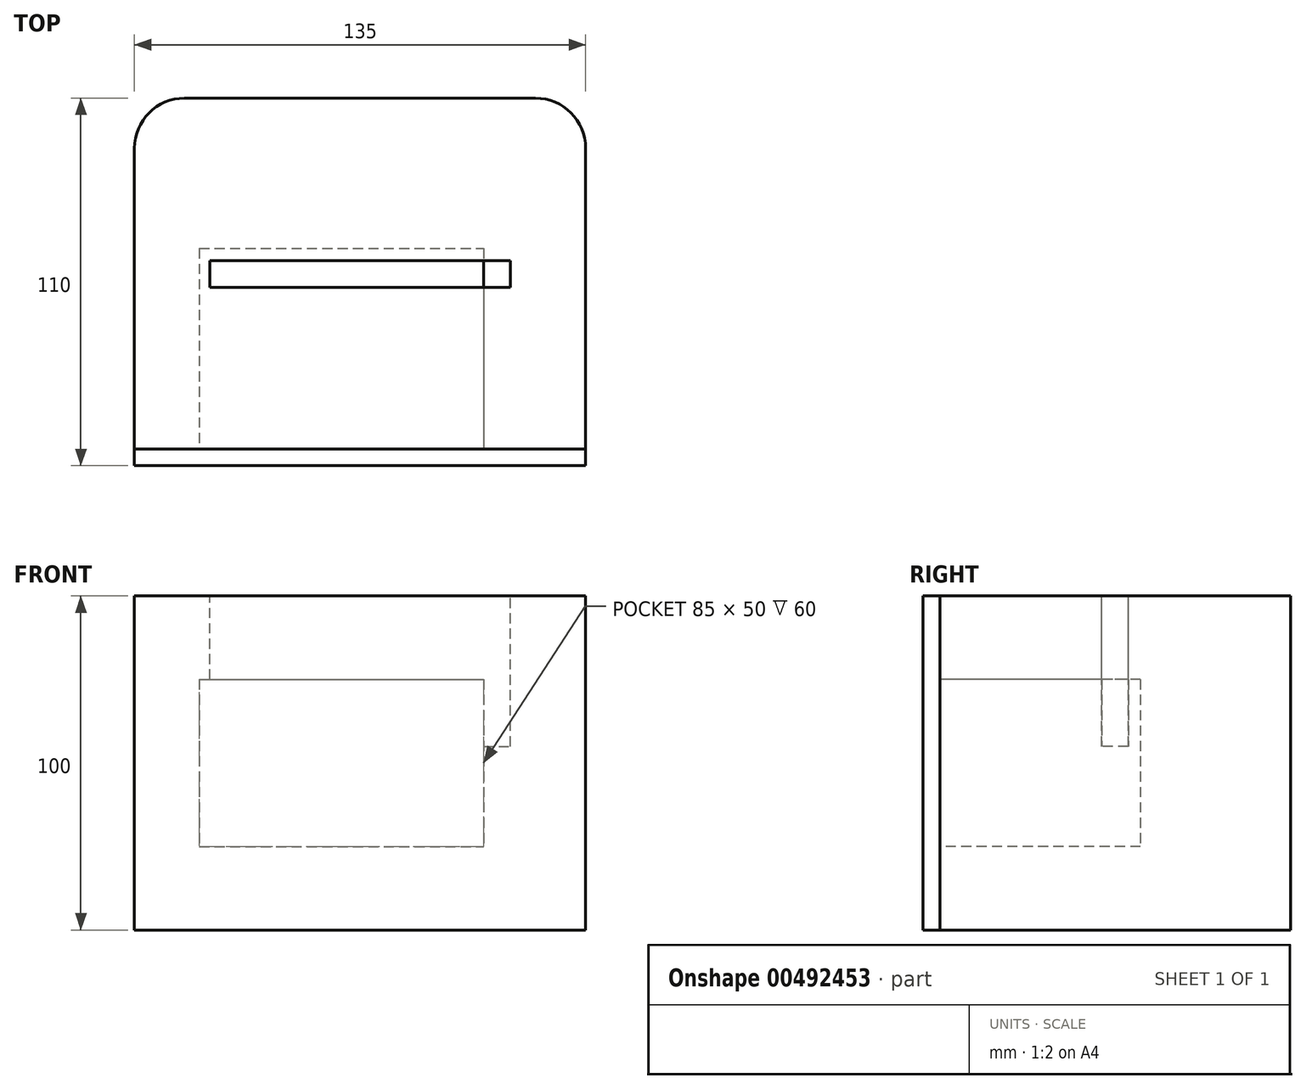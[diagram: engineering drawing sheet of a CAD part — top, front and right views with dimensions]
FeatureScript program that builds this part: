
annotation { "Feature Type Name" : "Feature", "Feature Type Description" : "" }
export const myFeature = defineFeature(function(context is Context, id is Id, definition is map)
    precondition{}
    {
        {
            var Q0;
            Q0=qCreatedBy(makeId("Front.planeOp"),FACE);
            var sketch = newSketch(context, id + "F0", { "sketchPlane" : qUnion([Q0])});
            skLineSegment(sketch, "E0.bottom", {"start": v(-67.5, 50) * mm, "end": v(67.5, 50) * mm});
            skLineSegment(sketch, "E0.top", {"start": v(-67.5, -50) * mm, "end": v(67.5, -50) * mm});
            skLineSegment(sketch, "E0.left", {"start": v(-67.5, 50) * mm, "end": v(-67.5, -50) * mm});
            skLineSegment(sketch, "E0.right", {"start": v(67.5, 50) * mm, "end": v(67.5, -50) * mm});
            skPoint(sketch, "E0.middle", {"position": v(0, 0) * mm});
            skSolve(sketch);
        }
        {
            var Q0;
            Q0 = qSketchRegion(id + "F0", true);
            extrude(context, id + "F1", {"entities" : qUnion([Q0]), "depth" : 105 * mm});
        }
        {
            var Q0;
            Q0=makeQuery(id+"F1.opExtrude","SWEPT_FACE",FACE,{"disambiguationData":[OSD([sQuery(id+"F0.wireOp",EDGE,"E0.bottom")])]});
            var sketch = newSketch(context, id + "F2", { "sketchPlane" : qUnion([Q0])});
            skLineSegment(sketch, "E1.bottom", {"start": v(-45, -48.62) * mm, "end": v(45, -48.62) * mm});
            skLineSegment(sketch, "E1.top", {"start": v(-45, -56.62) * mm, "end": v(45, -56.62) * mm});
            skLineSegment(sketch, "E1.left", {"start": v(-45, -48.62) * mm, "end": v(-45, -56.62) * mm});
            skLineSegment(sketch, "E1.right", {"start": v(45, -48.62) * mm, "end": v(45, -56.62) * mm});
            skPoint(sketch, "E1.middle", {"position": v(0, -52.62) * mm});
            skPoint(sketch, "E1.middle.positionSnap0", {"position": v(0, -105) * mm});
            skPoint(sketch, "E1.centerSnap0", {"position": v(0, -105) * mm});
            skSolve(sketch);
        }
        {
            var Q0;
            Q0 = qSketchRegion(id + "F2", true);
            extrude(context, id + "F3", {"entities" : qUnion([Q0]), "operationType" : NewBodyOperationType.REMOVE, "oppositeDirection" : true, "depth" : 45 * mm});
        }
        {
            var Q0;
            Q0=makeQuery(id+"F1.opExtrude","CAP_FACE",FACE,{"disambiguationData":[OSD([sQuery(id+"F0.wireOp",EDGE,"E0.bottom"),sQuery(id+"F0.wireOp",EDGE,"E0.top"),sQuery(id+"F0.wireOp",EDGE,"E0.left"),sQuery(id+"F0.wireOp",EDGE,"E0.right")])],"isStart":false});
            var sketch = newSketch(context, id + "F4", { "sketchPlane" : qUnion([Q0])});
            skLineSegment(sketch, "E2.bottom", {"start": v(-48.09, 25) * mm, "end": v(36.91, 25) * mm});
            skLineSegment(sketch, "E2.top", {"start": v(-48.09, -25) * mm, "end": v(36.91, -25) * mm});
            skLineSegment(sketch, "E2.left", {"start": v(-48.09, 25) * mm, "end": v(-48.09, -25) * mm});
            skLineSegment(sketch, "E2.right", {"start": v(36.91, 25) * mm, "end": v(36.91, -25) * mm});
            skPoint(sketch, "E2.middle", {"position": v(-5.59, 0) * mm});
            skSolve(sketch);
        }
        {
            var Q0;
            Q0 = qSketchRegion(id + "F4", true);
            extrude(context, id + "F5", {"entities" : qUnion([Q0]), "operationType" : NewBodyOperationType.REMOVE, "oppositeDirection" : true, "depth" : 60 * mm});
        }
        {
            var Q0;
            Q0=makeQuery(id+"F1.opExtrude","CAP_FACE",FACE,{"disambiguationData":[OSD([sQuery(id+"F0.wireOp",EDGE,"E0.bottom"),sQuery(id+"F0.wireOp",EDGE,"E0.top"),sQuery(id+"F0.wireOp",EDGE,"E0.left"),sQuery(id+"F0.wireOp",EDGE,"E0.right")])],"isStart":false});
            var sketch = newSketch(context, id + "F6", { "sketchPlane" : qUnion([Q0])});
            skLineSegment(sketch, "E3.bottom", {"start": v(67.5, 50) * mm, "end": v(-67.5, 50) * mm});
            skLineSegment(sketch, "E3.top", {"start": v(67.5, -50) * mm, "end": v(-67.5, -50) * mm});
            skLineSegment(sketch, "E3.left", {"start": v(67.5, 50) * mm, "end": v(67.5, -50) * mm});
            skLineSegment(sketch, "E3.right", {"start": v(-67.5, 50) * mm, "end": v(-67.5, -50) * mm});
            skSolve(sketch);
        }
        {
            var Q0;
            Q0 = qSketchRegion(id + "F6", true);
            extrude(context, id + "F7", {"entities" : qUnion([Q0]), "depth" : 5 * mm});
        }
        {
            var Q0;
            Q0=makeQuery(id+"F1.opExtrude","CAP_EDGE",EDGE,{"disambiguationData":[OSD([sQuery(id+"F0.wireOp",EDGE,"E0.left")])],"isStart":true});
            fillet(context, id + "F8", {"entities" : qUnion([Q0]), "radius" : 15 * mm, "tangentPropagation" : true, "allowEdgeOverflow" : false});
        }
        {
            var Q0;
            Q0=makeQuery(id+"F1.opExtrude","CAP_EDGE",EDGE,{"disambiguationData":[OSD([sQuery(id+"F0.wireOp",EDGE,"E0.right")])],"isStart":true});
            fillet(context, id + "F9", {"entities" : qUnion([Q0]), "radius" : 15 * mm, "tangentPropagation" : true, "allowEdgeOverflow" : false});
        }
    });
